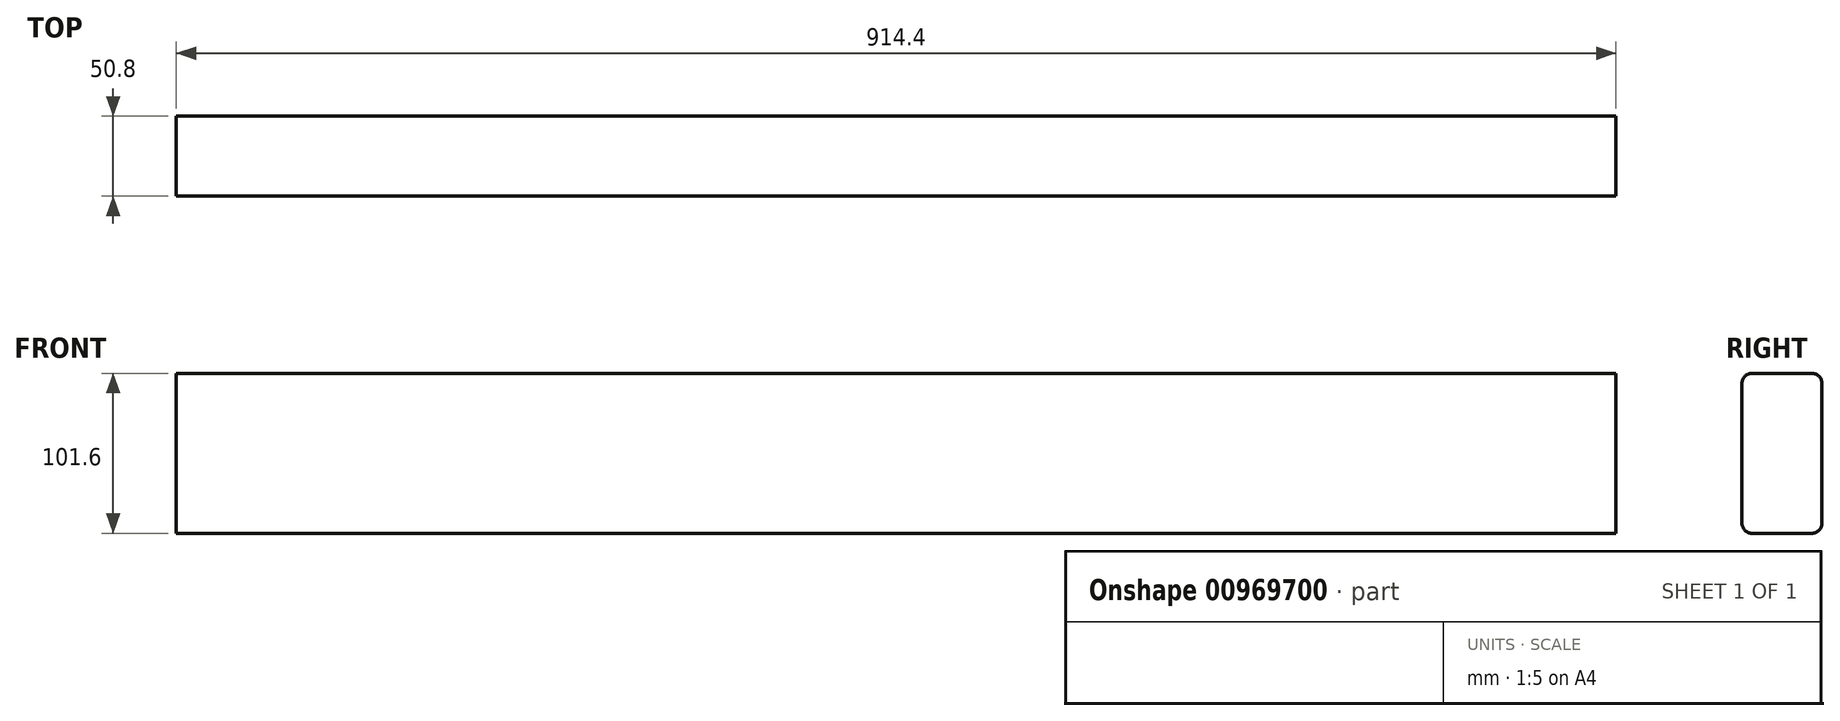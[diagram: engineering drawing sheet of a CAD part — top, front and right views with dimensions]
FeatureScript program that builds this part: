
annotation { "Feature Type Name" : "Feature", "Feature Type Description" : "" }
export const myFeature = defineFeature(function(context is Context, id is Id, definition is map)
    precondition{}
    {
        {
            var Q0;
            Q0=qCreatedBy(makeId("Right.planeOp"),FACE);
            var sketch = newSketch(context, id + "F0", { "sketchPlane" : qUnion([Q0])});
            skLineSegment(sketch, "E0.bottom", {"start": v(-25.4, -50.8) * mm, "end": v(25.4, -50.8) * mm});
            skLineSegment(sketch, "E0.top", {"start": v(-25.4, 50.8) * mm, "end": v(25.4, 50.8) * mm});
            skLineSegment(sketch, "E0.left", {"start": v(-25.4, -50.8) * mm, "end": v(-25.4, 50.8) * mm});
            skLineSegment(sketch, "E0.right", {"start": v(25.4, -50.8) * mm, "end": v(25.4, 50.8) * mm});
            skPoint(sketch, "E0.middle", {"position": v(0, 0) * mm});
            skSolve(sketch);
        }
        {
            var Q0;
            Q0=makeQuery(id+"F0.imprint","IMPRINT",FACE,{"disambiguationData":[TD([[makeQuery(id+"F0.imprint","IMPRINT",EDGE,{"derivedFrom":sQuery(id+"F0.wireOp",EDGE,"E0.bottom")}),1.0]])]});
            extrude(context, id + "F1", {"entities" : qUnion([Q0]), "endBound" : BoundingType.SYMMETRIC, "depth" : 914.4 * mm, "offsetDistance" : 25.4 * mm});
        }
        {
            var Q0;
            Q0=makeQuery(id+"F1.opExtrude","SWEPT_EDGE",EDGE,{"disambiguationData":[OSD([sQuery(id+"F0.wireOp",EDGE,"E0.bottom"),sQuery(id+"F0.wireOp",EDGE,"E0.left")])]});
            var Q1;
            Q1=makeQuery(id+"F1.opExtrude","SWEPT_EDGE",EDGE,{"disambiguationData":[OSD([sQuery(id+"F0.wireOp",EDGE,"E0.bottom"),sQuery(id+"F0.wireOp",EDGE,"E0.right")])]});
            var Q2;
            Q2=makeQuery(id+"F1.opExtrude","SWEPT_EDGE",EDGE,{"disambiguationData":[OSD([sQuery(id+"F0.wireOp",EDGE,"E0.top"),sQuery(id+"F0.wireOp",EDGE,"E0.left")])]});
            var Q3;
            Q3=makeQuery(id+"F1.opExtrude","SWEPT_EDGE",EDGE,{"disambiguationData":[OSD([sQuery(id+"F0.wireOp",EDGE,"E0.top"),sQuery(id+"F0.wireOp",EDGE,"E0.right")])]});
            fillet(context, id + "F2", {"entities" : qUnion([Q0, Q1, Q2, Q3]), "radius" : 6.35 * mm, "tangentPropagation" : true, "allowEdgeOverflow" : false});
        }
    });
